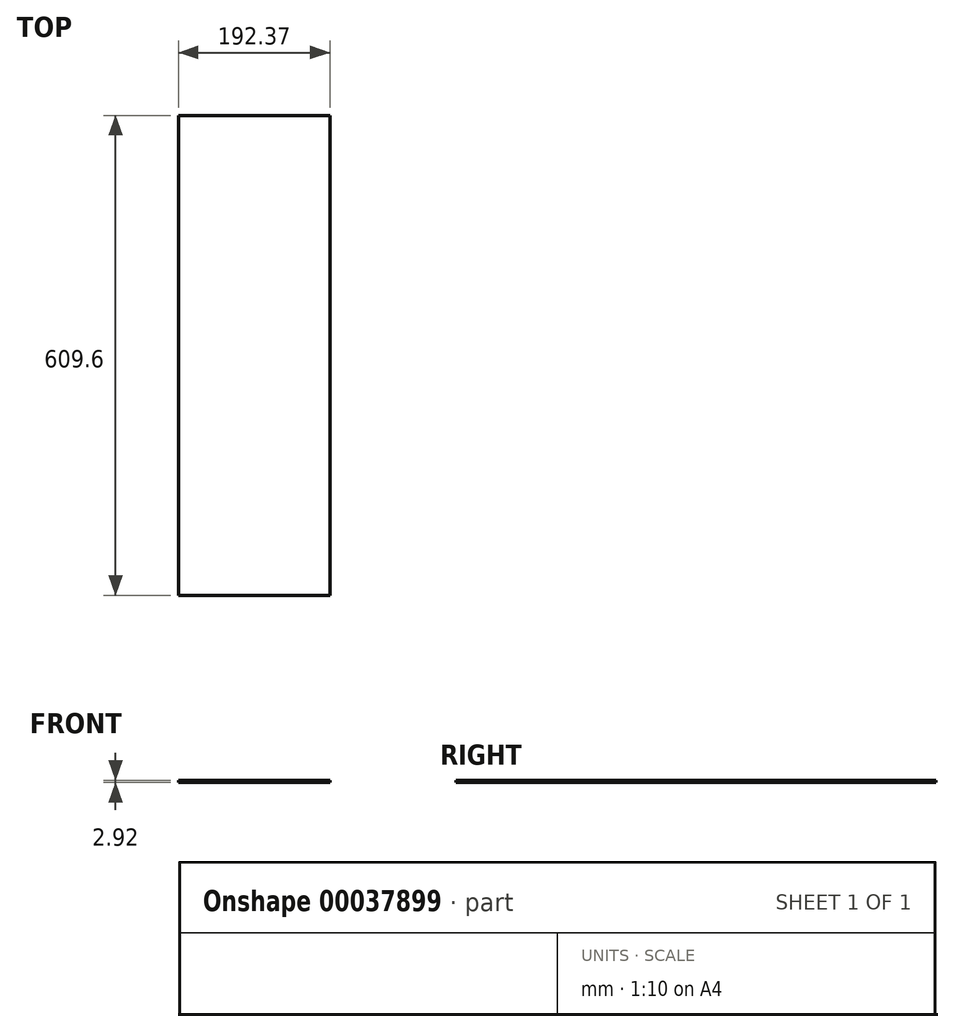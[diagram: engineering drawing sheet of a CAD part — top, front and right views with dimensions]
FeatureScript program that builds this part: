
annotation { "Feature Type Name" : "Feature", "Feature Type Description" : "" }
export const myFeature = defineFeature(function(context is Context, id is Id, definition is map)
    precondition{}
    {
        {
            var Q0;
            Q0=qCreatedBy(makeId("Top.planeOp"),FACE);
            var sketch = newSketch(context, id + "F0", { "sketchPlane" : qUnion([Q0])});
            skLineSegment(sketch, "E0.bottom", {"start": v(0, 0) * mm, "end": v(192.37, 0) * mm});
            skLineSegment(sketch, "E0.top", {"start": v(0, -609.6) * mm, "end": v(192.37, -609.6) * mm});
            skLineSegment(sketch, "E0.left", {"start": v(0, 0) * mm, "end": v(0, -609.6) * mm});
            skLineSegment(sketch, "E0.right", {"start": v(192.37, 0) * mm, "end": v(192.37, -609.6) * mm});
            skSolve(sketch);
        }
        {
            var Q0;
            Q0 = qSketchRegion(id + "F0", true);
            extrude(context, id + "F1", {"entities" : qUnion([Q0]), "depth" : 2.92 * mm});
        }
    });
